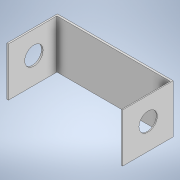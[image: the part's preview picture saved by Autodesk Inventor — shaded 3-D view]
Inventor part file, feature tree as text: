
AUTODESK INVENTOR PART (.ipt)
format: ipt  version: 2020 (Build 240168000, 168)  size: 116,224 bytes
history: native  units: in
note: dims shown in document units (in); Inventor stores cm internally (conversion verified against a paired STEP export)
features: sketch x4, extrude x2, hole x1
ambient origin geometry x8: Origin, YZ Plane, XZ Plane, XY Plane, X Axis, Y Axis, Z Axis, Center Point
bodies: Solid1 (feature_tree)
feature tree (7):
  extrude  "Extrusion1"  Depth=3.937in TaperAngle=0.0deg
  sketch  "Sketch3"  dims[d28=0.625in d29=0.625in d30=0.75in d31=0.188in d32=90.0deg d33=1.029in d34=0.8108in d35=1.6535in d36=0.0in]
  hole  "Hole4"  [1 undecoded]
  extrude  "Extrusion4"  Depth=0.75in
  sketch  "Sketch1"  dims[d0=1.6535in d1=3.937in d2=0.0in]
  sketch  "Sketch8"  dims[d37=0.0625in d38=0.75in]
  sketch  "Sketch9"  dims[d39=0.375in]
note: 1 required parameter value undecoded (feature->parameter linkage not recoverable at this tier; creation-order binding heuristic only, values carry confidence <= 0.55)
